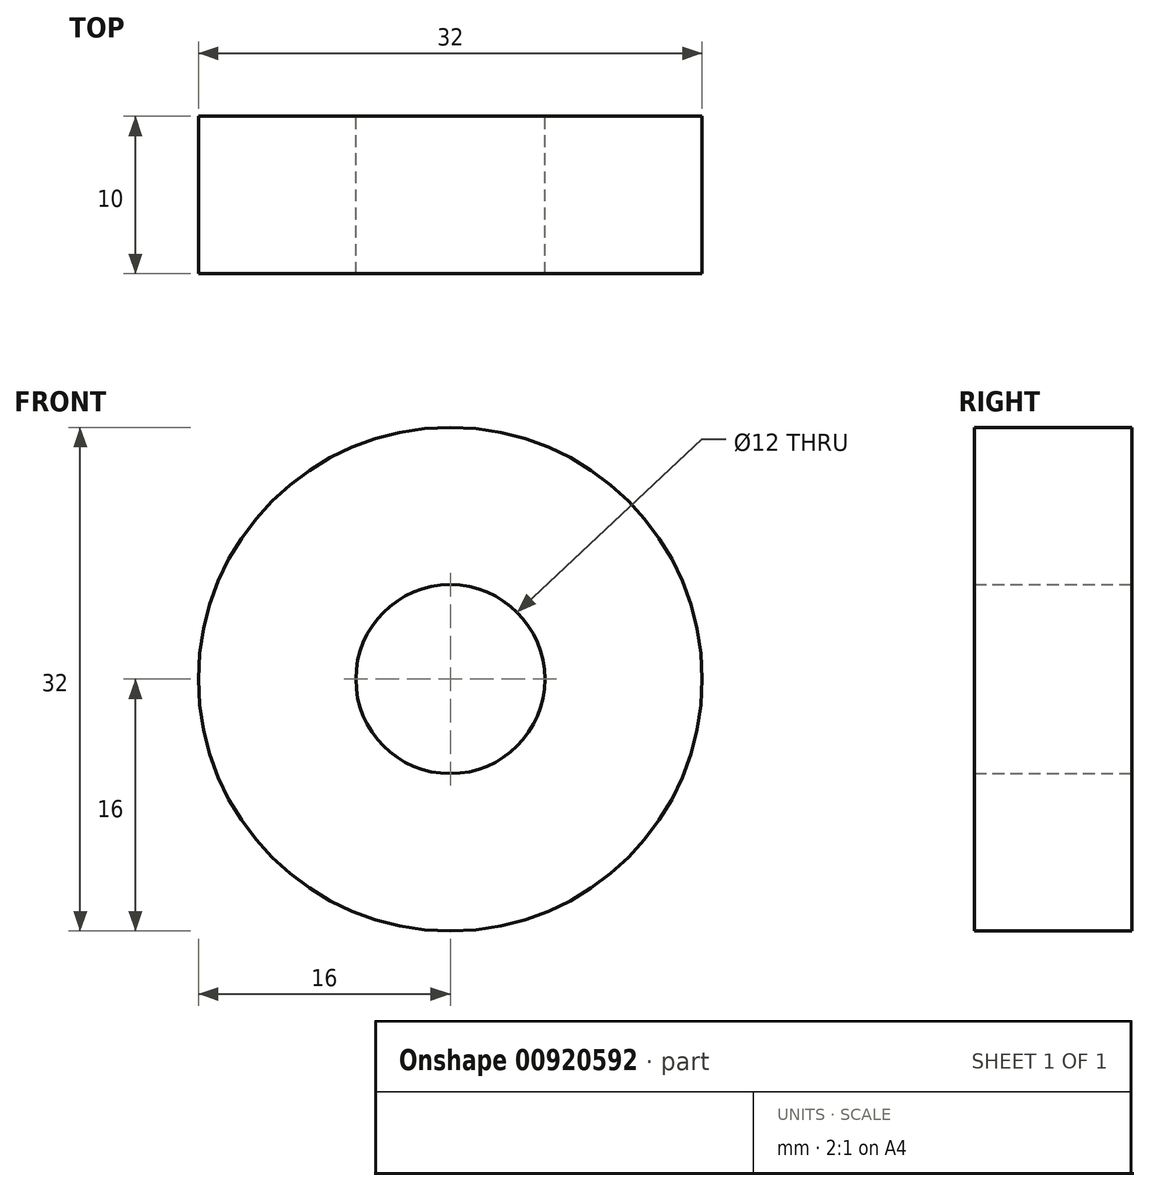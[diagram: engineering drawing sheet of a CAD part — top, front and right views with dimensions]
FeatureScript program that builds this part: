
annotation { "Feature Type Name" : "Feature", "Feature Type Description" : "" }
export const myFeature = defineFeature(function(context is Context, id is Id, definition is map)
    precondition{}
    {
        {
            var Q0;
            Q0=qCreatedBy(makeId("Front.planeOp"),FACE);
            var sketch = newSketch(context, id + "F0", { "sketchPlane" : qUnion([Q0])});
            skCircle(sketch, "E0", {"center": v(0, 0) * mm, "radius": 16 * mm});
            skCircle(sketch, "E1", {"center": v(0, 0) * mm, "radius": 6 * mm});
            skSolve(sketch);
        }
        {
            var Q0;
            Q0=makeQuery(id+"F0.imprint","IMPRINT",FACE,{"disambiguationData":[TD([[makeQuery(id+"F0.imprint","IMPRINT",EDGE,{"derivedFrom":sQuery(id+"F0.wireOp",EDGE,"E0")}),1.0]])]});
            extrude(context, id + "F1", {"entities" : qUnion([Q0]), "depth" : 10 * mm, "offsetDistance" : 25 * mm, "symmetric" : true});
        }
    });
